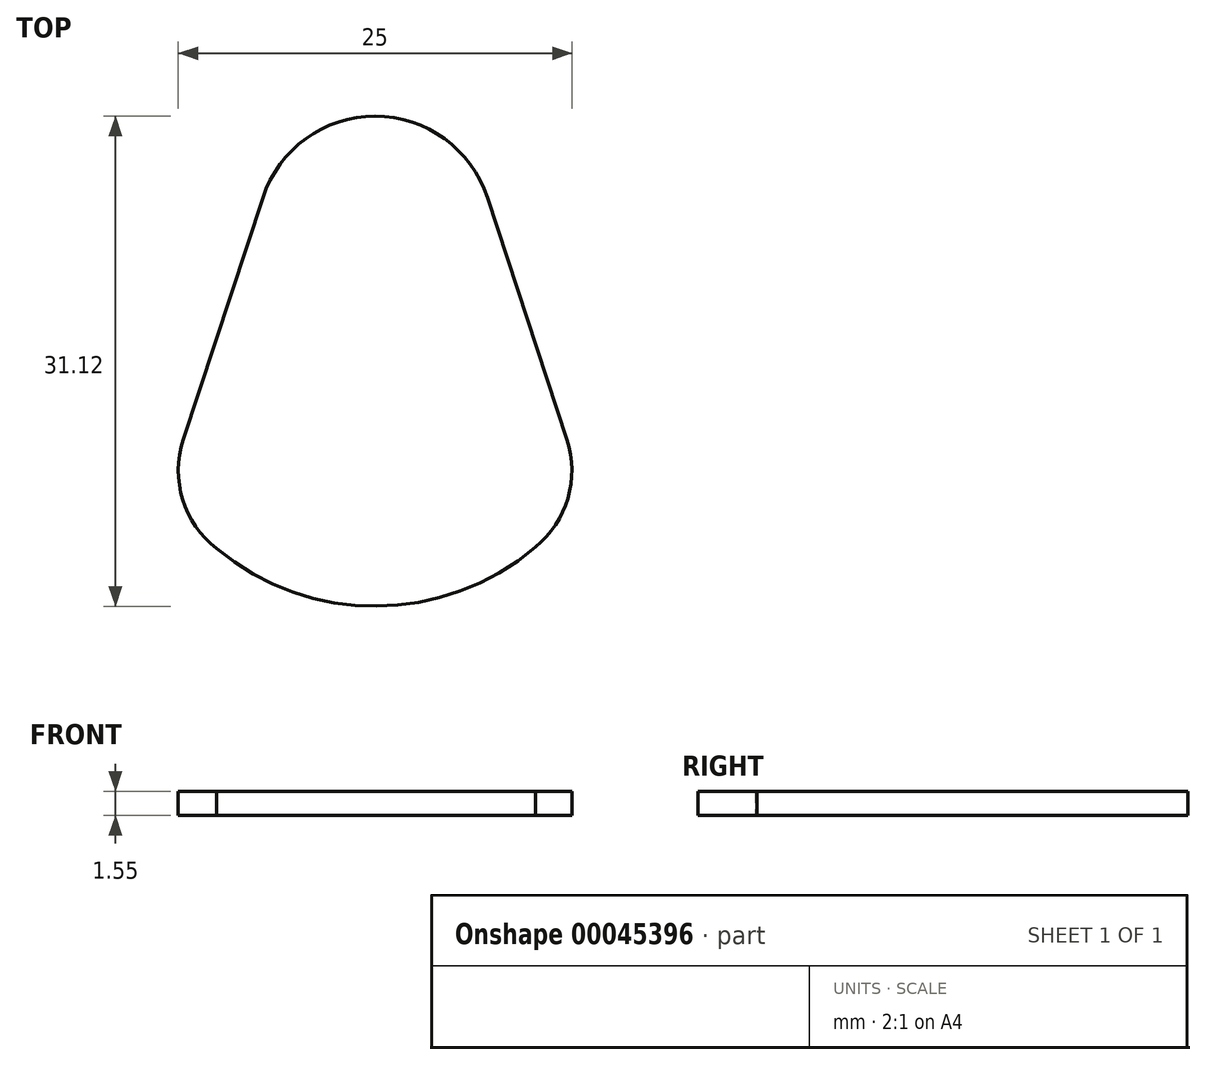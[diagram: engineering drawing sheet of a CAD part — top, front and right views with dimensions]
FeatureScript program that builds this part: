
annotation { "Feature Type Name" : "Feature", "Feature Type Description" : "" }
export const myFeature = defineFeature(function(context is Context, id is Id, definition is map)
    precondition{}
    {
        {
            var Q0;
            Q0=qCreatedBy(makeId("Top.planeOp"),FACE);
            var sketch = newSketch(context, id + "F0", { "sketchPlane" : qUnion([Q0])});
            skPoint(sketch, "E0.rect.middle", {"position": v(0, 0) * mm});
            skPoint(sketch, "E1", {"position": v(0, 7.5) * mm});
            skArc(sketch, "E2", {"start": v(7.12, 9.84) * mm, "mid": v(0, 15) * mm, "end": v(-7.12, 9.84) * mm});
            skLineSegment(sketch, "E3", {"start": v(-7.12, 9.84) * mm, "end": v(-12.19, -5.55) * mm});
            skLineSegment(sketch, "E4", {"start": v(7.12, 9.84) * mm, "end": v(12.19, -5.55) * mm});
            skPoint(sketch, "E5.orphan", {"position": v(-12.5, 15) * mm});
            skPoint(sketch, "E6.orphan", {"position": v(12.5, 15) * mm});
            skPoint(sketch, "E7.orphan", {"position": v(-12.5, -15) * mm});
            skPoint(sketch, "E0.rect.left.start.orphan", {"position": v(12.5, -15) * mm});
            skPoint(sketch, "E8", {"position": v(0, -7.5) * mm});
            skPoint(sketch, "E9", {"position": v(-6.25, -7.5) * mm});
            skArc(sketch, "E10", {"start": v(-12.19, -5.55) * mm, "mid": v(-12.22, -9.34) * mm, "end": v(-10.06, -12.45) * mm});
            skPoint(sketch, "E11", {"position": v(6.25, -7.5) * mm});
            skArc(sketch, "E12", {"start": v(10.18, -12.36) * mm, "mid": v(12.25, -9.27) * mm, "end": v(12.19, -5.55) * mm});
            skArc(sketch, "E13", {"start": v(-10.06, -12.45) * mm, "mid": v(0.08, -16.12) * mm, "end": v(10.18, -12.36) * mm});
            skSolve(sketch);
        }
        {
            var Q0;
            Q0=makeQuery(id+"F0.imprint","IMPRINT",FACE,{"disambiguationData":[TD([[makeQuery(id+"F0.imprint","IMPRINT",EDGE,{"derivedFrom":sQuery(id+"F0.wireOp",EDGE,"E2")}),1.0]])]});
            extrude(context, id + "F1", {"entities" : qUnion([Q0]), "depth" : 1.55 * mm});
        }
    });
